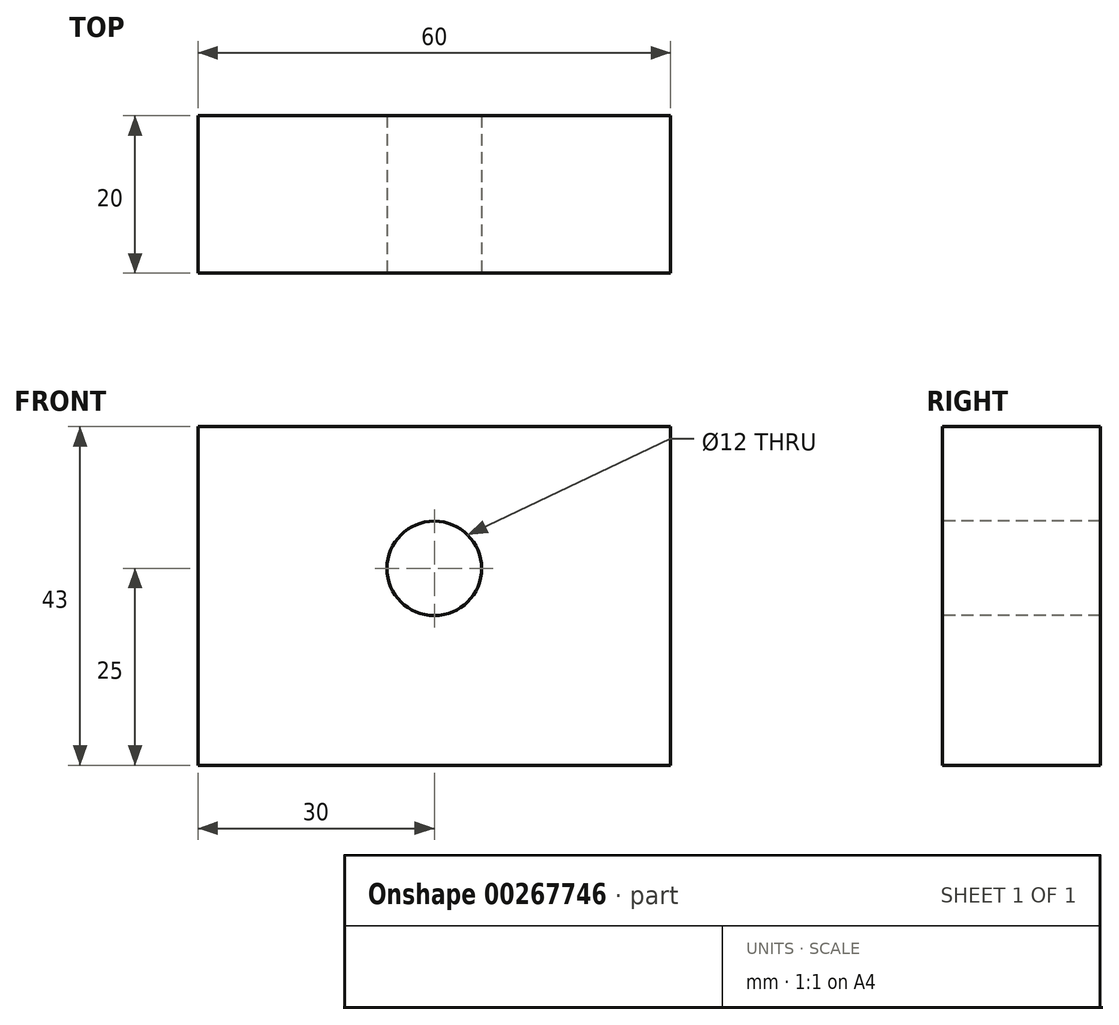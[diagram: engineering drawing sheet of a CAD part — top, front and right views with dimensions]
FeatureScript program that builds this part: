
annotation { "Feature Type Name" : "Feature", "Feature Type Description" : "" }
export const myFeature = defineFeature(function(context is Context, id is Id, definition is map)
    precondition{}
    {
        {
            var Q0;
            Q0=qCreatedBy(makeId("Front.planeOp"),FACE);
            var sketch = newSketch(context, id + "F0", { "sketchPlane" : qUnion([Q0])});
            skLineSegment(sketch, "E0.bottom", {"start": v(30, 21.5) * mm, "end": v(-30, 21.5) * mm});
            skLineSegment(sketch, "E0.top", {"start": v(30, -21.5) * mm, "end": v(-30, -21.5) * mm});
            skLineSegment(sketch, "E0.left", {"start": v(30, 21.5) * mm, "end": v(30, -21.5) * mm});
            skLineSegment(sketch, "E0.right", {"start": v(-30, 21.5) * mm, "end": v(-30, -21.5) * mm});
            skPoint(sketch, "E0.middle", {"position": v(0, 0) * mm});
            skLineSegment(sketch, "E1", {"start": v(0, -21.5) * mm, "end": v(0, 3.5) * mm, "construction": true});
            skPoint(sketch, "E1.endSnap0", {"position": v(0, -21.5) * mm});
            skCircle(sketch, "E2", {"center": v(0, 3.5) * mm, "radius": 6 * mm});
            skSolve(sketch);
        }
        {
            var Q0;
            Q0 = qSketchRegion(id + "F0", true);
            extrude(context, id + "F1", {"entities" : qUnion([Q0]), "oppositeDirection" : true, "depth" : 20 * mm});
        }
    });
